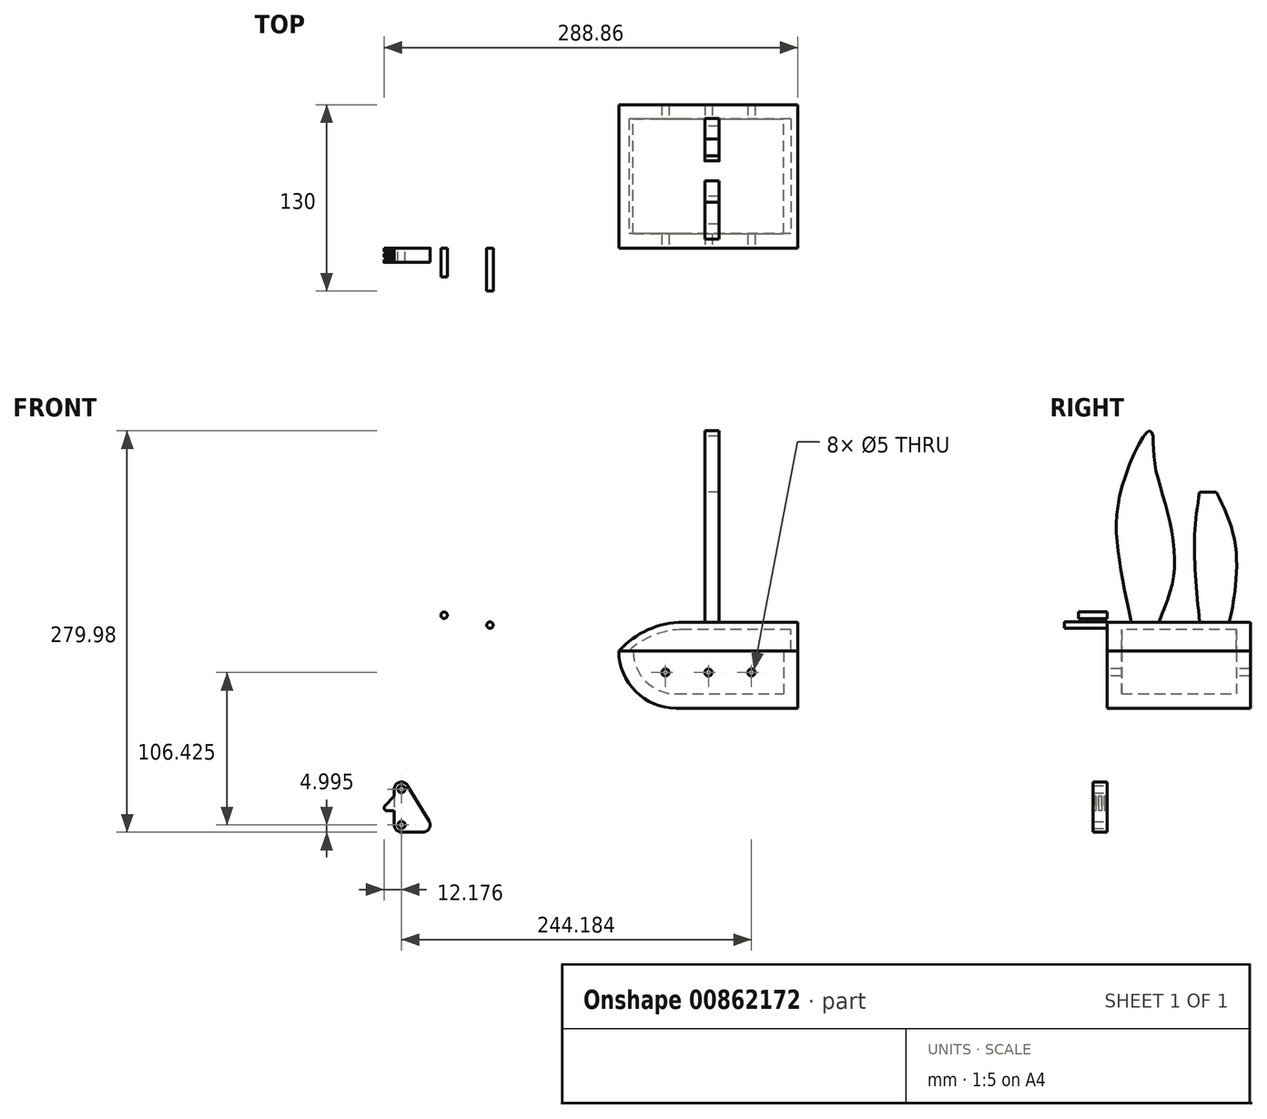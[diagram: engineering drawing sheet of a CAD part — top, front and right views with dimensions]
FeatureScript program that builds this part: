
annotation { "Feature Type Name" : "Feature", "Feature Type Description" : "" }
export const myFeature = defineFeature(function(context is Context, id is Id, definition is map)
    precondition{}
    {
        {
            var Q0;
            Q0=qCreatedBy(makeId("Top.planeOp"),FACE);
            var sketch = newSketch(context, id + "F0", { "sketchPlane" : qUnion([Q0])});
            skLineSegment(sketch, "E0.bottom", {"start": v(0, 0) * mm, "end": v(125, 0) * mm});
            skLineSegment(sketch, "E0.top", {"start": v(0, 100) * mm, "end": v(125, 100) * mm});
            skLineSegment(sketch, "E0.left", {"start": v(0, 0) * mm, "end": v(0, 100) * mm});
            skLineSegment(sketch, "E0.right", {"start": v(125, 0) * mm, "end": v(125, 100) * mm});
            skLineSegment(sketch, "E1.bottom", {"start": v(10, 10) * mm, "end": v(115, 10) * mm});
            skLineSegment(sketch, "E1.top", {"start": v(10, 90) * mm, "end": v(115, 90) * mm});
            skLineSegment(sketch, "E1.left", {"start": v(10, 10) * mm, "end": v(10, 90) * mm});
            skLineSegment(sketch, "E1.right", {"start": v(115, 10) * mm, "end": v(115, 90) * mm});
            skSolve(sketch);
        }
        {
            var Q0;
            Q0=makeQuery(id+"F0.imprint","IMPRINT",FACE,{"disambiguationData":[TD([[makeQuery(id+"F0.imprint","IMPRINT",EDGE,{"derivedFrom":sQuery(id+"F0.wireOp",EDGE,"E0.bottom")}),1.0]])]});
            extrude(context, id + "F1", {"entities" : qUnion([Q0]), "depth" : 30 * mm, "offsetDistance" : 25 * mm});
        }
        {
            var Q0;
            Q0=makeQuery(id+"F1.opExtrude","SWEPT_FACE",FACE,{"disambiguationData":[OSD([sQuery(id+"F0.wireOp",EDGE,"E0.bottom")])]});
            var sketch = newSketch(context, id + "F2", { "sketchPlane" : qUnion([Q0])});
            skCircle(sketch, "E2", {"center": v(62.5, 15) * mm, "radius": 2.5 * mm});
            skCircle(sketch, "E3", {"center": v(92.5, 15) * mm, "radius": 2.5 * mm});
            skCircle(sketch, "E4", {"center": v(32.5, 15) * mm, "radius": 2.5 * mm});
            skSolve(sketch);
        }
        {
            var Q0;
            Q0=makeQuery(id+"F2.imprint","IMPRINT",FACE,{"disambiguationData":[TD([[makeQuery(id+"F2.imprint","IMPRINT",EDGE,{"derivedFrom":sQuery(id+"F2.wireOp",EDGE,"E4")}),1.0]])]});
            var Q1;
            Q1=makeQuery(id+"F2.imprint","IMPRINT",FACE,{"disambiguationData":[TD([[makeQuery(id+"F2.imprint","IMPRINT",EDGE,{"derivedFrom":sQuery(id+"F2.wireOp",EDGE,"E2")}),1.0]])]});
            var Q2;
            Q2=makeQuery(id+"F2.imprint","IMPRINT",FACE,{"disambiguationData":[TD([[makeQuery(id+"F2.imprint","IMPRINT",EDGE,{"derivedFrom":sQuery(id+"F2.wireOp",EDGE,"E3")}),1.0]])]});
            extrude(context, id + "F3", {"entities" : qUnion([Q0, Q1, Q2]), "operationType" : NewBodyOperationType.REMOVE, "endBound" : BoundingType.THROUGH_ALL, "oppositeDirection" : true, "depth" : 25 * mm, "offsetDistance" : 25 * mm});
        }
        {
            var Q0;
            Q0=makeQuery(id+"F1.opExtrude","CAP_FACE",FACE,{"disambiguationData":[OSD([sQuery(id+"F0.wireOp",EDGE,"E0.bottom"),sQuery(id+"F0.wireOp",EDGE,"E0.top"),sQuery(id+"F0.wireOp",EDGE,"E0.left"),sQuery(id+"F0.wireOp",EDGE,"E0.right"),sQuery(id+"F0.wireOp",EDGE,"E1.bottom"),sQuery(id+"F0.wireOp",EDGE,"E1.top"),sQuery(id+"F0.wireOp",EDGE,"E1.left"),sQuery(id+"F0.wireOp",EDGE,"E1.right")])],"isStart":true});
            var sketch = newSketch(context, id + "F4", { "sketchPlane" : qUnion([Q0])});
            skLineSegment(sketch, "E5.bottom", {"start": v(0, 0) * mm, "end": v(125, 0) * mm});
            skLineSegment(sketch, "E5.top", {"start": v(0, -100) * mm, "end": v(125, -100) * mm});
            skLineSegment(sketch, "E5.left", {"start": v(0, 0) * mm, "end": v(0, -100) * mm});
            skLineSegment(sketch, "E5.right", {"start": v(125, 0) * mm, "end": v(125, -100) * mm});
            skSolve(sketch);
        }
        {
            var Q0;
            Q0=makeQuery(id+"F4.imprint","IMPRINT",FACE,{"disambiguationData":[TD([[makeQuery(id+"F4.imprint","IMPRINT",EDGE,{"derivedFrom":sQuery(id+"F4.wireOp",EDGE,"E5.bottom")}),-1.0]])]});
            var Q1;
            Q1=makeQuery(id+"F4.imprint","IMPRINT",FACE,{"disambiguationData":[TD([[makeQuery(id+"F4.imprint","IMPRINT",EDGE,{"derivedFrom":makeQuery(id+"F1.opExtrude","CAP_EDGE",EDGE,{"disambiguationData":[OSD([sQuery(id+"F0.wireOp",EDGE,"E1.bottom")])],"isStart":true})}),-1.0]])]});
            extrude(context, id + "F5", {"entities" : qUnion([Q0, Q1]), "operationType" : NewBodyOperationType.ADD, "depth" : 10 * mm, "offsetDistance" : 25 * mm});
        }
        {
            var Q0;
            Q0=makeQuery(id+"F5.boolean.opBoolean","MERGE",FACE,{"derivedFrom":[makeQuery(id+"F1.opExtrude","SWEPT_FACE",FACE,{"disambiguationData":[OSD([sQuery(id+"F0.wireOp",EDGE,"E0.bottom")])]}),makeQuery(id+"F5.opExtrude","SWEPT_FACE",FACE,{"disambiguationData":[OSD([sQuery(id+"F4.wireOp",EDGE,"E5.bottom")])]})]});
            var sketch = newSketch(context, id + "F6", { "sketchPlane" : qUnion([Q0])});
            skArc(sketch, "E6", {"start": v(0, 30) * mm, "mid": v(11.72, 1.72) * mm, "end": v(40, -10) * mm});
            skLineSegment(sketch, "E7", {"start": v(0, 30) * mm, "end": v(-36.86, 33.31) * mm});
            skLineSegment(sketch, "E8", {"start": v(-36.86, 33.31) * mm, "end": v(-29.77, -57.2) * mm});
            skLineSegment(sketch, "E9", {"start": v(-29.77, -57.2) * mm, "end": v(40, -10) * mm});
            skSolve(sketch);
        }
        {
            var Q0;
            Q0=makeQuery(id+"F6.imprint","IMPRINT",FACE,{"disambiguationData":[TD([[makeQuery(id+"F6.imprint","IMPRINT",EDGE,{"derivedFrom":sQuery(id+"F6.wireOp",EDGE,"E7")}),1.0]])]});
            var Q1;
            {var subQ0=sQuery(id+"F6.wireOp",EDGE,"E6");Q1=makeQuery(id+"F6.imprint","IMPRINT",FACE,{"disambiguationData":[TD([[makeQuery(id+"F6.imprint","IMPRINT",EDGE,{"derivedFrom":subQ0}),-1.0]])]});}
            extrude(context, id + "F7", {"entities" : qUnion([Q0, Q1]), "operationType" : NewBodyOperationType.REMOVE, "oppositeDirection" : true, "depth" : 6666 * mm, "offsetDistance" : 25 * mm});
        }
        {
            var Q0;
            Q0=makeQuery(id+"F1.opExtrude","SWEPT_FACE",FACE,{"disambiguationData":[OSD([sQuery(id+"F0.wireOp",EDGE,"E1.top")])]});
            var sketch = newSketch(context, id + "F8", { "sketchPlane" : qUnion([Q0])});
            skArc(sketch, "E10.0", {"start": v(0, 30) * mm, "mid": v(11.72, 1.72) * mm, "end": v(40, -10) * mm});
            skLineSegment(sketch, "E11", {"start": v(0, 30) * mm, "end": v(10, 30) * mm});
            skLineSegment(sketch, "E12", {"start": v(40, -10) * mm, "end": v(40, 0) * mm});
            skArc(sketch, "E13.0", {"start": v(10, 30) * mm, "mid": v(18.79, 8.79) * mm, "end": v(40, 0) * mm});
            skSolve(sketch);
        }
        {
            var Q0;
            {var subQ5=sQuery(id+"F8.wireOp",EDGE,"E13.0");Q0=makeQuery(id+"F8.imprint","IMPRINT",FACE,{"disambiguationData":[TD([[makeQuery(id+"F8.imprint","IMPRINT",EDGE,{"derivedFrom":subQ5}),-1.0]])]});}
            extrude(context, id + "F9", {"entities" : qUnion([Q0]), "operationType" : NewBodyOperationType.ADD, "depth" : 83.4 * mm, "offsetDistance" : 25 * mm});
        }
        {
            var Q0;
            Q0=makeQuery(id+"F5.boolean.opBoolean","MERGE",FACE,{"derivedFrom":[makeQuery(id+"F1.opExtrude","SWEPT_FACE",FACE,{"disambiguationData":[OSD([sQuery(id+"F0.wireOp",EDGE,"E0.bottom")])]}),makeQuery(id+"F5.opExtrude","SWEPT_FACE",FACE,{"disambiguationData":[OSD([sQuery(id+"F4.wireOp",EDGE,"E5.bottom")])]})]});
            var sketch = newSketch(context, id + "F10", { "sketchPlane" : qUnion([Q0])});
            skLineSegment(sketch, "E14.bottom", {"start": v(125, 30) * mm, "end": v(45, 30) * mm});
            skLineSegment(sketch, "E14.top", {"start": v(125, 50) * mm, "end": v(45, 50) * mm});
            skLineSegment(sketch, "E14.left", {"start": v(125, 30) * mm, "end": v(125, 50) * mm});
            skLineSegment(sketch, "E14.right", {"start": v(45, 30) * mm, "end": v(45, 50) * mm});
            skArc(sketch, "E15", {"start": v(45, 50) * mm, "mid": v(20.38, 44.77) * mm, "end": v(0, 30) * mm});
            skSolve(sketch);
        }
        {
            var Q0;
            {var subQ0=sQuery(id+"F10.wireOp",EDGE,"E14.right");Q0=makeQuery(id+"F10.imprint","IMPRINT",FACE,{"disambiguationData":[TD([[makeQuery(id+"F10.imprint","IMPRINT",EDGE,{"derivedFrom":subQ0}),1.0]])]});}
            var Q1;
            Q1=makeQuery(id+"F10.imprint","IMPRINT",FACE,{"disambiguationData":[TD([[makeQuery(id+"F10.imprint","IMPRINT",EDGE,{"derivedFrom":sQuery(id+"F10.wireOp",EDGE,"E14.bottom")}),1.0]])]});
            extrude(context, id + "F11", {"entities" : qUnion([Q0, Q1]), "oppositeDirection" : true, "depth" : 100 * mm, "offsetDistance" : 25 * mm});
        }
        {
            var Q0;
            Q0=qCreatedBy(makeId("Right.planeOp"),FACE);
            cPlane(context, id + "F12", {"entities" : qUnion([Q0]), "cplaneType" : CPlaneType.OFFSET, "offset" : 60 * mm, "width" : 150 * mm, "height" : 150 * mm});
        }
        {
            var Q0;
            Q0=qCreatedBy(makeId("Front.planeOp"),FACE);
            cPlane(context, id + "F13", {"entities" : qUnion([Q0]), "cplaneType" : CPlaneType.OFFSET, "offset" : 50 * mm, "oppositeDirection" : true, "width" : 150 * mm, "height" : 150 * mm});
        }
        {
            var Q0;
            Q0=qCreatedBy(id+"F12.planeOp",FACE);
            var sketch = newSketch(context, id + "F14", { "sketchPlane" : qUnion([Q0])});
            skFitSpline(sketch, "E16", {"points": [v(85, 49.83) * mm, v(88.38, 66.62) * mm, v(89.24, 105.05) * mm, v(76.14, 140.9) * mm], "startDerivative": vector(13.93, 58.73) * mm, "endDerivative": vector(-44.11, 91.16) * mm});
            skLineSegment(sketch, "E17", {"start": v(76.14, 140.9) * mm, "end": v(64.48, 140.9) * mm});
            skFitSpline(sketch, "E18", {"points": [v(64.48, 140.9) * mm, v(61.06, 113.59) * mm, v(61.63, 82.85) * mm, v(64.48, 49.83) * mm], "startDerivative": vector(-13.6, -84.92) * mm, "endDerivative": vector(9.07, -95.38) * mm});
            skLineSegment(sketch, "E19", {"start": v(85, 49.83) * mm, "end": v(64.48, 49.83) * mm});
            skFitSpline(sketch, "E20", {"points": [v(36.04, 50) * mm, v(45.96, 79.9) * mm, v(43.95, 119.35) * mm, v(33.88, 156.58) * mm, v(32.07, 179.92) * mm], "startDerivative": vector(47.9, 129.75) * mm, "endDerivative": vector(-0.7, 106.5) * mm});
            skFitSpline(sketch, "E21", {"points": [v(16.7, 50) * mm, v(7.12, 103.05) * mm, v(11.14, 147.52) * mm, v(29.26, 183.55) * mm, v(32.07, 179.92) * mm], "startDerivative": vector(-35.74, 181.88) * mm, "endDerivative": vector(23.64, -61.48) * mm});
            skLineSegment(sketch, "E22", {"start": v(36.04, 50) * mm, "end": v(16.7, 50) * mm});
            skSolve(sketch);
        }
        {
            var Q0;
            Q0=makeQuery(id+"F14.imprint","IMPRINT",FACE,{"disambiguationData":[TD([[makeQuery(id+"F14.imprint","IMPRINT",EDGE,{"derivedFrom":sQuery(id+"F14.wireOp",EDGE,"E16")}),1.0]])]});
            var Q1;
            Q1=makeQuery(id+"F14.imprint","IMPRINT",FACE,{"disambiguationData":[TD([[makeQuery(id+"F14.imprint","IMPRINT",EDGE,{"derivedFrom":sQuery(id+"F14.wireOp",EDGE,"E20")}),1.0]])]});
            extrude(context, id + "F15", {"entities" : qUnion([Q0, Q1]), "operationType" : NewBodyOperationType.ADD, "depth" : 10 * mm, "offsetDistance" : 25 * mm});
        }
        {
            var Q0;
            Q0=qCreatedBy(id+"F13.planeOp",FACE);
            var sketch = newSketch(context, id + "F16", { "sketchPlane" : qUnion([Q0])});
            skArc(sketch, "E23.0", {"start": v(45, 50) * mm, "mid": v(20.38, 44.77) * mm, "end": v(0, 30) * mm});
            skLineSegment(sketch, "E24.0", {"start": v(125, 50) * mm, "end": v(45, 50) * mm});
            skArc(sketch, "E25.0", {"start": v(45, 45) * mm, "mid": v(24.57, 41.11) * mm, "end": v(7, 30) * mm});
            skLineSegment(sketch, "E25.1", {"start": v(120, 45) * mm, "end": v(45, 45) * mm});
            skLineSegment(sketch, "E26.0", {"start": v(120, 30) * mm, "end": v(120, 45) * mm});
            skLineSegment(sketch, "E27", {"start": v(120, 30) * mm, "end": v(7, 30) * mm});
            skSolve(sketch);
        }
        {
            var Q0;
            Q0=qSketchRegion(id+"F16",true);
            extrude(context, id + "F17", {"entities" : qUnion([Q0]), "operationType" : NewBodyOperationType.REMOVE, "oppositeDirection" : true, "depth" : 40 * mm, "offsetDistance" : 25 * mm, "hasSecondDirection" : true, "secondDirectionOppositeDirection" : false, "secondDirectionDepth" : 40 * mm});
        }
        {
            var Q0;
            Q0=qCreatedBy(makeId("Front.planeOp"),FACE);
            var sketch = newSketch(context, id + "F18", { "sketchPlane" : qUnion([Q0])});
            skLineSegment(sketch, "E28", {"start": v(-156.68, -66.42) * mm, "end": v(-156.68, -91.42) * mm});
            skArc(sketch, "E29", {"start": v(-156.68, -91.42) * mm, "mid": v(-155.22, -94.96) * mm, "end": v(-151.68, -96.42) * mm});
            skLineSegment(sketch, "E30", {"start": v(-151.68, -96.42) * mm, "end": v(-136.68, -96.42) * mm});
            skArc(sketch, "E31", {"start": v(-136.68, -96.42) * mm, "mid": v(-132.33, -93.89) * mm, "end": v(-132.4, -88.85) * mm});
            skArc(sketch, "E32", {"start": v(-147.4, -63.85) * mm, "mid": v(-153.02, -61.6) * mm, "end": v(-156.68, -66.42) * mm});
            skLineSegment(sketch, "E33", {"start": v(-132.4, -88.85) * mm, "end": v(-147.4, -63.85) * mm});
            skCircle(sketch, "E34", {"center": v(-151.68, -66.42) * mm, "radius": 2.5 * mm});
            skCircle(sketch, "E35", {"center": v(-151.68, -91.42) * mm, "radius": 2.5 * mm});
            skSolve(sketch);
        }
        {
            var Q0;
            Q0=makeQuery(id+"F18.imprint","IMPRINT",FACE,{"disambiguationData":[TD([[makeQuery(id+"F18.imprint","IMPRINT",EDGE,{"derivedFrom":sQuery(id+"F18.wireOp",EDGE,"E28")}),1.0]])]});
            extrude(context, id + "F19", {"entities" : qUnion([Q0]), "depth" : 10 * mm, "offsetDistance" : 25 * mm});
        }
        {
            var Q0;
            Q0=makeQuery(id+"F19.opExtrude","CAP_FACE",FACE,{"disambiguationData":[OSD([sQuery(id+"F18.wireOp",EDGE,"E28"),sQuery(id+"F18.wireOp",EDGE,"E29"),sQuery(id+"F18.wireOp",EDGE,"E30"),sQuery(id+"F18.wireOp",EDGE,"E31"),sQuery(id+"F18.wireOp",EDGE,"E32"),sQuery(id+"F18.wireOp",EDGE,"E33"),sQuery(id+"F18.wireOp",EDGE,"E34"),sQuery(id+"F18.wireOp",EDGE,"E35")])],"isStart":false});
            var sketch = newSketch(context, id + "F20", { "sketchPlane" : qUnion([Q0])});
            skLineSegment(sketch, "E36", {"start": v(-156.68, -71.42) * mm, "end": v(-163.27, -78.01) * mm});
            skLineSegment(sketch, "E37", {"start": v(-161.86, -81.42) * mm, "end": v(-156.68, -81.42) * mm});
            skPoint(sketch, "E38.visualSharp", {"position": v(-166.68, -81.42) * mm});
            skArc(sketch, "E38.filletArc", {"start": v(-163.27, -78.01) * mm, "mid": v(-163.7, -80.2) * mm, "end": v(-161.86, -81.42) * mm});
            skSolve(sketch);
        }
        {
            var Q0;
            {var subQ0=sQuery(id+"F20.wireOp",EDGE,"E36");Q0=makeQuery(id+"F20.imprint","IMPRINT",FACE,{"disambiguationData":[TD([[makeQuery(id+"F20.imprint","IMPRINT",EDGE,{"derivedFrom":subQ0}),1.0]])]});}
            extrude(context, id + "F21", {"entities" : qUnion([Q0]), "operationType" : NewBodyOperationType.ADD, "oppositeDirection" : true, "depth" : 10 * mm, "offsetDistance" : 25 * mm});
        }
        {
            var Q0;
            Q0=makeQuery(id+"F21.opExtrude","SWEPT_FACE",FACE,{"disambiguationData":[OSD([sQuery(id+"F20.wireOp",EDGE,"E37")])]});
            var sketch = newSketch(context, id + "F22", { "sketchPlane" : qUnion([Q0])});
            skLineSegment(sketch, "E39.bottom", {"start": v(-156.68, 2) * mm, "end": v(-173.13, 2) * mm});
            skLineSegment(sketch, "E39.top", {"start": v(-156.68, 4) * mm, "end": v(-173.13, 4) * mm});
            skLineSegment(sketch, "E39.left", {"start": v(-156.68, 2) * mm, "end": v(-156.68, 4) * mm});
            skLineSegment(sketch, "E39.right", {"start": v(-173.13, 2) * mm, "end": v(-173.13, 4) * mm});
            skLineSegment(sketch, "E40.bottom", {"start": v(-156.68, 6) * mm, "end": v(-173.76, 6) * mm});
            skLineSegment(sketch, "E40.top", {"start": v(-156.68, 8) * mm, "end": v(-173.76, 8) * mm});
            skLineSegment(sketch, "E40.left", {"start": v(-156.68, 6) * mm, "end": v(-156.68, 8) * mm});
            skLineSegment(sketch, "E40.right", {"start": v(-173.76, 6) * mm, "end": v(-173.76, 8) * mm});
            skSolve(sketch);
        }
        {
            var Q0;
            {var subQ0=sQuery(id+"F22.wireOp",EDGE,"E40.right");Q0=makeQuery(id+"F22.imprint","IMPRINT",FACE,{"disambiguationData":[TD([[makeQuery(id+"F22.imprint","IMPRINT",EDGE,{"derivedFrom":subQ0}),-1.0]])]});}
            var Q1;
            {var subQ0=sQuery(id+"F22.wireOp",EDGE,"E39.left");Q1=makeQuery(id+"F22.imprint","IMPRINT",FACE,{"disambiguationData":[TD([[makeQuery(id+"F22.imprint","IMPRINT",EDGE,{"derivedFrom":subQ0}),1.0]])]});}
            var Q2;
            {var subQ0=sQuery(id+"F22.wireOp",EDGE,"E40.left");Q2=makeQuery(id+"F22.imprint","IMPRINT",FACE,{"disambiguationData":[TD([[makeQuery(id+"F22.imprint","IMPRINT",EDGE,{"derivedFrom":subQ0}),1.0]])]});}
            var Q3;
            {var subQ0=sQuery(id+"F22.wireOp",EDGE,"E39.right");Q3=makeQuery(id+"F22.imprint","IMPRINT",FACE,{"disambiguationData":[TD([[makeQuery(id+"F22.imprint","IMPRINT",EDGE,{"derivedFrom":subQ0}),-1.0]])]});}
            extrude(context, id + "F23", {"entities" : qUnion([Q0, Q1, Q2, Q3]), "operationType" : NewBodyOperationType.REMOVE, "oppositeDirection" : true, "depth" : 25 * mm, "offsetDistance" : 25 * mm});
        }
        {
            var Q0;
            Q0=qCreatedBy(makeId("Front.planeOp"),FACE);
            var sketch = newSketch(context, id + "F24", { "sketchPlane" : qUnion([Q0])});
            skCircle(sketch, "E41", {"center": v(-121.94, 54.92) * mm, "radius": 2.25 * mm});
            skSolve(sketch);
        }
        {
            var Q0;
            Q0=makeQuery(id+"F24.imprint","IMPRINT",FACE,{"disambiguationData":[TD([[makeQuery(id+"F24.imprint","IMPRINT",EDGE,{"derivedFrom":sQuery(id+"F24.wireOp",EDGE,"E41")}),1.0]])]});
            extrude(context, id + "F25", {"entities" : qUnion([Q0]), "depth" : 20 * mm, "offsetDistance" : 25 * mm});
        }
        {
            var Q0;
            Q0=qCreatedBy(makeId("Front.planeOp"),FACE);
            var sketch = newSketch(context, id + "F26", { "sketchPlane" : qUnion([Q0])});
            skCircle(sketch, "E42", {"center": v(-89.93, 48.05) * mm, "radius": 2.25 * mm});
            skSolve(sketch);
        }
        {
            var Q0;
            Q0=makeQuery(id+"F26.imprint","IMPRINT",FACE,{"disambiguationData":[TD([[makeQuery(id+"F26.imprint","IMPRINT",EDGE,{"derivedFrom":sQuery(id+"F26.wireOp",EDGE,"E42")}),1.0]])]});
            extrude(context, id + "F27", {"entities" : qUnion([Q0]), "depth" : 30 * mm, "offsetDistance" : 25 * mm});
        }
    });
